# Revit family: Barrisol Rail BMS 345-20
name_source: partatom
category: Modèles génériques
revit_build: Autodesk Revit 2018 (Build: 20170223_1515(x64)
units: mm (PartAtom-declared; Revit-internal decimal feet)

## family parameters
Cote de connecteur circulaire = Utiliser le diamètre
Couper avec des vides une fois chargée = Non
Hôte = Face
Partagée = Non
Peut héberger une armature = Non
Point de calcul de pièce = Non
Type d'élément = Normal

## types (1)
- BMS 345-20
    Barrisol BMS 345-20 = BMS 345-20
    Description = Arcolis by Barrisol
    Diametre = 500 mm  [stored 1.64042 ft]
    Diametre led = 240 mm
    Diamtre Membrane 1 = 470 mm
    Diamtre Membrane 2 = 235 mm  [stored 0.770997 ft]
    Elévation par défaut = 0 mm  [stored 0 ft]
    Fabricant = Barrisol
    Image du type = <Aucun>
    Membrane 1 = TISSUS
    Membrane 2 = TISSUS
    Modèle = Barrisol BMS 345-20
    Note d'identification = BMS 345-20
    Rail = Aluminium
    URL = https://barrisol.com

note: [stored X ft] marks values corroborated as IEEE doubles in the binary element streams (Revit-internal decimal feet)

## geometry (parser evidence)
native form markers: Blend x4
no freeform markers — native parametric forms only
